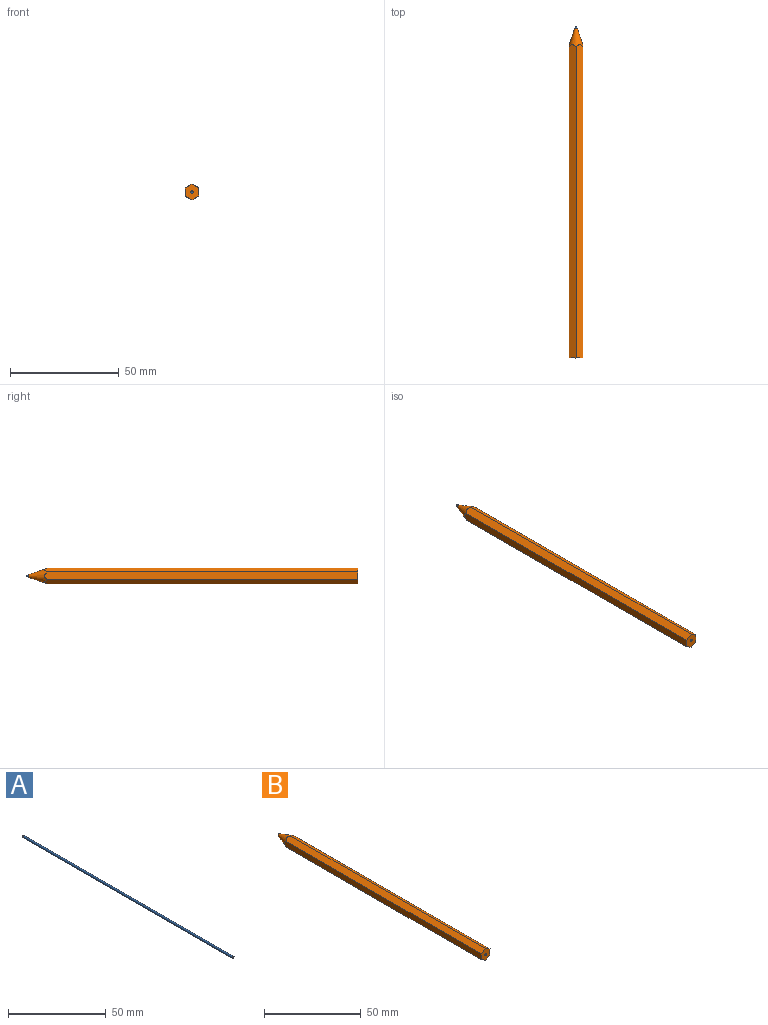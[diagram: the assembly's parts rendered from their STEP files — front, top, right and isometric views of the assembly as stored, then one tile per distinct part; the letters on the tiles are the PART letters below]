
ASSEMBLY  parts=2 mates=1
PART A: 4 faces, bbox 1.3x152.4x1.3 mm
  f0: cylinder r=0.63mm len=151.14mm, axis (0,1,0), area 602mm2, adj f1,f2
  f1: plane 1.27x1.27mm, normal (0,-1,0), area 1.3mm2, adj f0
  f2: cone r=0.2mm half-angle=19.1deg, axis (0,-1,0), area 3.5mm2, adj f0,f3
  f3: plane 0.39x0.39mm, normal (0,1,0), area 0.1mm2, adj f2
PART B: 9 faces, bbox 7.3x151.1x7.3 mm
  f0: plane 143.82x3.18mm, normal (-0.5,0,0.87), area 525.5mm2, adj f1,f5,f7,f8
  f1: plane 143.82x3.67mm, normal (-1,0,0), area 525.5mm2, adj f0,f2,f7,f8
  f2: plane 143.82x3.17mm, normal (-0.5,0,-0.87), area 525.5mm2, adj f1,f3,f7,f8
  f3: plane 143.82x3.18mm, normal (0.5,0,-0.87), area 525.5mm2, adj f2,f4,f7,f8
  f4: plane 143.82x3.67mm, normal (1,0,0), area 525.5mm2, adj f3,f5,f7,f8
  f5: plane 143.82x3.17mm, normal (0.5,0,0.87), area 525.5mm2, adj f0,f4,f7,f8
  f6: cylinder r=0.64mm len=151.14mm, axis (0,1,0), area 603mm2, adj f7,f8
  f7: plane 7.33x6.35mm, normal (0,-1,0), area 33.7mm2, adj f0,f1,f2,f3,f4,f5,f6
  f8: cone r=0.2mm half-angle=19.1deg, axis (0,-1,0), area 102.6mm2, adj f0,f1,f2,f3,f4,f5,f6
PLACE A t=(-34.07,38.07,-28.64)mm
PLACE B t=(-34.07,38.07,-28.64)mm
MATE cylindrical A.f0 <-> B.f6  axis (0,-1,0) through (-34.07,-114.33,-28.64)mm
